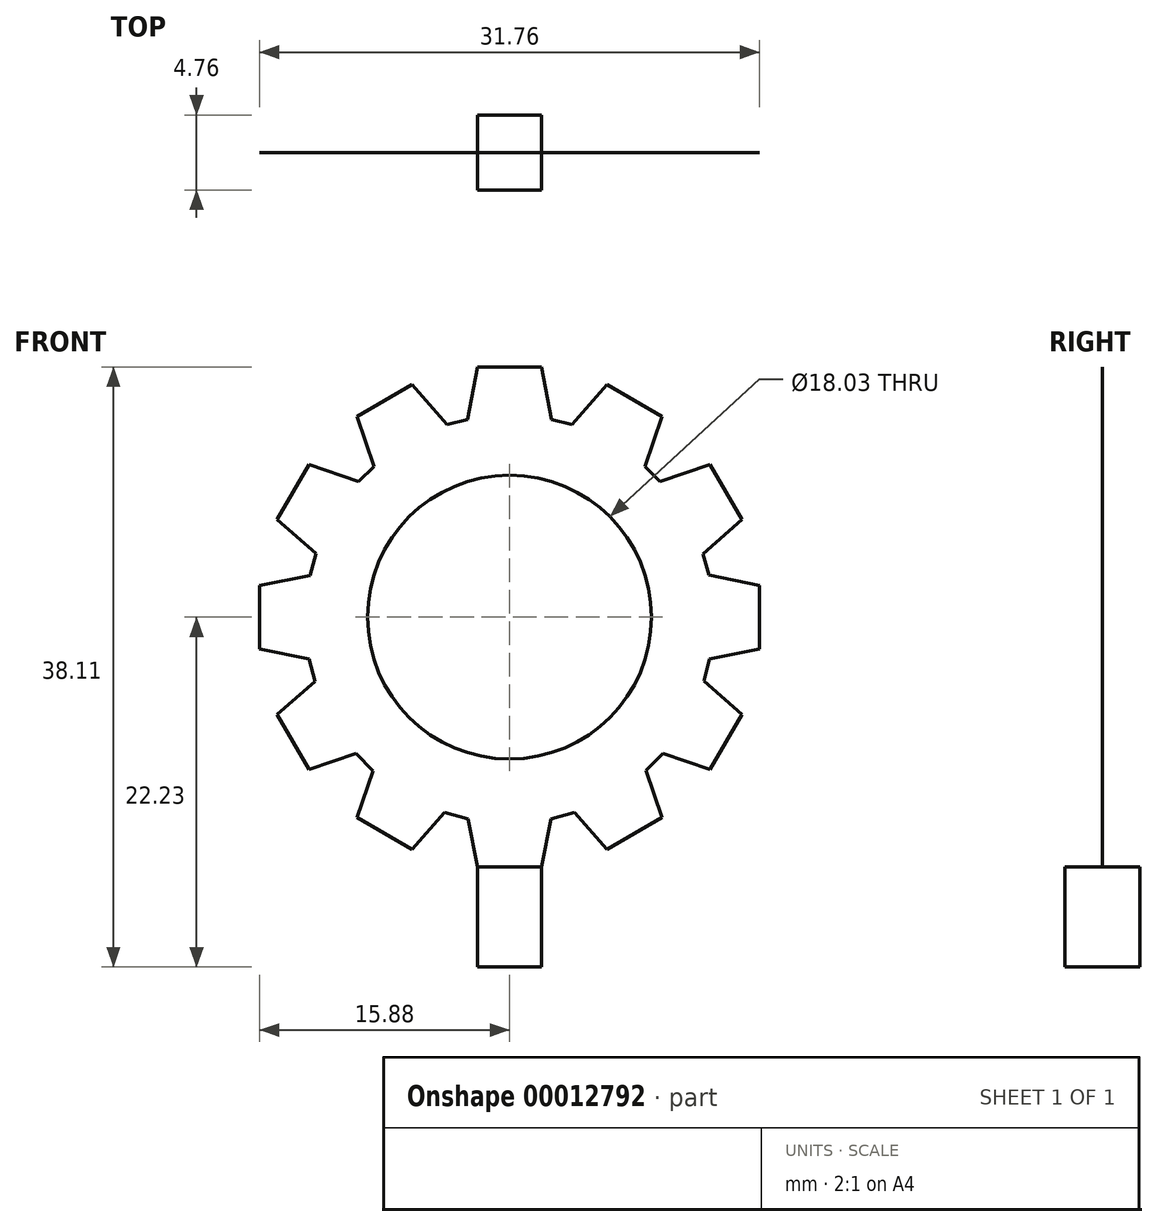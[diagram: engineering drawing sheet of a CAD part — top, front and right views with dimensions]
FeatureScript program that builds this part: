
annotation { "Feature Type Name" : "Feature", "Feature Type Description" : "" }
export const myFeature = defineFeature(function(context is Context, id is Id, definition is map)
    precondition{}
    {
        {
            var Q0;
            Q0=qCreatedBy(makeId("Front.planeOp"),FACE);
            var sketch = newSketch(context, id + "F0", { "sketchPlane" : qUnion([Q0])});
            skArc(sketch, "E0", {"start": v(0, 9.01) * mm, "mid": v(-6.37, 6.37) * mm, "end": v(-9.01, 0) * mm});
            skArc(sketch, "E1", {"start": v(-9.01, 0) * mm, "mid": v(-6.37, -6.37) * mm, "end": v(0, -9.01) * mm});
            skArc(sketch, "E2", {"start": v(0, -9.01) * mm, "mid": v(6.37, -6.37) * mm, "end": v(9.01, 0) * mm});
            skArc(sketch, "E3", {"start": v(9.01, 0) * mm, "mid": v(6.37, 6.37) * mm, "end": v(0, 9.01) * mm});
            skLineSegment(sketch, "E4", {"start": v(12.28, 4.01) * mm, "end": v(14.76, 6.19) * mm});
            skLineSegment(sketch, "E5", {"start": v(14.76, 6.19) * mm, "end": v(12.74, 9.69) * mm});
            skLineSegment(sketch, "E6", {"start": v(12.74, 9.69) * mm, "end": v(9.57, 8.6) * mm});
            skLineSegment(sketch, "E7", {"start": v(9.57, 8.6) * mm, "end": v(8.6, 9.56) * mm});
            skLineSegment(sketch, "E8", {"start": v(8.6, 9.56) * mm, "end": v(9.69, 12.74) * mm});
            skLineSegment(sketch, "E9", {"start": v(9.69, 12.74) * mm, "end": v(6.19, 14.76) * mm});
            skLineSegment(sketch, "E10", {"start": v(6.19, 14.76) * mm, "end": v(3.96, 12.22) * mm});
            skLineSegment(sketch, "E11", {"start": v(3.96, 12.22) * mm, "end": v(2.68, 12.56) * mm});
            skLineSegment(sketch, "E12", {"start": v(2.68, 12.56) * mm, "end": v(2.02, 15.88) * mm});
            skLineSegment(sketch, "E13", {"start": v(2.02, 15.88) * mm, "end": v(-2.02, 15.88) * mm});
            skLineSegment(sketch, "E14", {"start": v(-2.02, 15.88) * mm, "end": v(-2.68, 12.56) * mm});
            skLineSegment(sketch, "E15", {"start": v(-2.68, 12.56) * mm, "end": v(-3.97, 12.22) * mm});
            skLineSegment(sketch, "E16", {"start": v(-3.97, 12.22) * mm, "end": v(-6.19, 14.76) * mm});
            skLineSegment(sketch, "E17", {"start": v(-6.19, 14.76) * mm, "end": v(-9.69, 12.74) * mm});
            skLineSegment(sketch, "E18", {"start": v(-9.69, 12.74) * mm, "end": v(-8.61, 9.57) * mm});
            skLineSegment(sketch, "E19", {"start": v(-8.61, 9.57) * mm, "end": v(-9.58, 8.62) * mm});
            skLineSegment(sketch, "E20", {"start": v(-9.58, 8.62) * mm, "end": v(-12.74, 9.69) * mm});
            skLineSegment(sketch, "E21", {"start": v(-12.74, 9.69) * mm, "end": v(-14.76, 6.19) * mm});
            skLineSegment(sketch, "E22", {"start": v(-14.76, 6.19) * mm, "end": v(-12.3, 4.03) * mm});
            skLineSegment(sketch, "E23", {"start": v(-12.3, 4.03) * mm, "end": v(-12.68, 2.66) * mm});
            skLineSegment(sketch, "E24", {"start": v(-12.68, 2.66) * mm, "end": v(-15.88, 2.02) * mm});
            skLineSegment(sketch, "E25", {"start": v(-15.88, 2.02) * mm, "end": v(-15.88, -2.02) * mm});
            skLineSegment(sketch, "E26", {"start": v(-15.88, -2.02) * mm, "end": v(-12.73, -2.65) * mm});
            skLineSegment(sketch, "E27", {"start": v(-12.73, -2.65) * mm, "end": v(-12.36, -4.08) * mm});
            skLineSegment(sketch, "E28", {"start": v(-12.36, -4.08) * mm, "end": v(-14.76, -6.19) * mm});
            skLineSegment(sketch, "E29", {"start": v(-14.76, -6.19) * mm, "end": v(-12.74, -9.69) * mm});
            skLineSegment(sketch, "E30", {"start": v(-12.74, -9.69) * mm, "end": v(-9.76, -8.68) * mm});
            skLineSegment(sketch, "E31", {"start": v(-9.76, -8.68) * mm, "end": v(-8.68, -9.77) * mm});
            skLineSegment(sketch, "E32", {"start": v(-8.68, -9.77) * mm, "end": v(-9.69, -12.74) * mm});
            skLineSegment(sketch, "E33", {"start": v(-9.69, -12.74) * mm, "end": v(-6.19, -14.76) * mm});
            skLineSegment(sketch, "E34", {"start": v(-6.19, -14.76) * mm, "end": v(-4.14, -12.42) * mm});
            skLineSegment(sketch, "E35", {"start": v(-4.14, -12.42) * mm, "end": v(-2.63, -12.83) * mm});
            skLineSegment(sketch, "E36", {"start": v(-2.63, -12.83) * mm, "end": v(-2.02, -15.88) * mm});
            skLineSegment(sketch, "E37", {"start": v(-2.02, -15.88) * mm, "end": v(2.02, -15.88) * mm});
            skLineSegment(sketch, "E38", {"start": v(2.02, -15.88) * mm, "end": v(2.63, -12.82) * mm});
            skLineSegment(sketch, "E39", {"start": v(2.63, -12.82) * mm, "end": v(4.13, -12.41) * mm});
            skLineSegment(sketch, "E40", {"start": v(4.13, -12.41) * mm, "end": v(6.19, -14.76) * mm});
            skLineSegment(sketch, "E41", {"start": v(6.19, -14.76) * mm, "end": v(9.69, -12.74) * mm});
            skLineSegment(sketch, "E42", {"start": v(9.69, -12.74) * mm, "end": v(8.67, -9.75) * mm});
            skLineSegment(sketch, "E43", {"start": v(8.67, -9.75) * mm, "end": v(9.74, -8.67) * mm});
            skLineSegment(sketch, "E44", {"start": v(9.74, -8.67) * mm, "end": v(12.74, -9.69) * mm});
            skLineSegment(sketch, "E45", {"start": v(12.74, -9.69) * mm, "end": v(14.76, -6.19) * mm});
            skLineSegment(sketch, "E46", {"start": v(14.76, -6.19) * mm, "end": v(12.34, -4.07) * mm});
            skLineSegment(sketch, "E47", {"start": v(12.34, -4.07) * mm, "end": v(12.7, -2.65) * mm});
            skLineSegment(sketch, "E48", {"start": v(12.7, -2.65) * mm, "end": v(15.87, -2.02) * mm});
            skLineSegment(sketch, "E49", {"start": v(15.87, -2.02) * mm, "end": v(15.88, 2.02) * mm});
            skLineSegment(sketch, "E50", {"start": v(15.88, 2.02) * mm, "end": v(12.65, 2.66) * mm});
            skLineSegment(sketch, "E51", {"start": v(12.65, 2.66) * mm, "end": v(12.28, 4.01) * mm});
            skSolve(sketch);
        }
        {
            var Q0;
            Q0=makeQuery(id+"F0.imprint","IMPRINT",FACE,{"disambiguationData":[TD([[makeQuery(id+"F0.imprint","IMPRINT",EDGE,{"derivedFrom":sQuery(id+"F0.wireOp",EDGE,"E0")}),-1.0]])]});
            extrude(context, id + "F1", {"entities" : qUnion([Q0]), "oppositeDirection" : true, "depth" : 3 / 406.4 * mm});
        }
        {
            var Q0;
            Q0=makeQuery(id+"F1.opExtrude","SWEPT_BODY",BODY,{"disambiguationData":[OSD([sQuery(id+"F0.wireOp",EDGE,"E0"),sQuery(id+"F0.wireOp",EDGE,"E1"),sQuery(id+"F0.wireOp",EDGE,"E2"),sQuery(id+"F0.wireOp",EDGE,"E3"),sQuery(id+"F0.wireOp",EDGE,"E4"),sQuery(id+"F0.wireOp",EDGE,"E5"),sQuery(id+"F0.wireOp",EDGE,"E6"),sQuery(id+"F0.wireOp",EDGE,"E7"),sQuery(id+"F0.wireOp",EDGE,"E8"),sQuery(id+"F0.wireOp",EDGE,"E9"),sQuery(id+"F0.wireOp",EDGE,"E10"),sQuery(id+"F0.wireOp",EDGE,"E11"),sQuery(id+"F0.wireOp",EDGE,"E12"),sQuery(id+"F0.wireOp",EDGE,"E13"),sQuery(id+"F0.wireOp",EDGE,"E14"),sQuery(id+"F0.wireOp",EDGE,"E15"),sQuery(id+"F0.wireOp",EDGE,"E16"),sQuery(id+"F0.wireOp",EDGE,"E17"),sQuery(id+"F0.wireOp",EDGE,"E18"),sQuery(id+"F0.wireOp",EDGE,"E19"),sQuery(id+"F0.wireOp",EDGE,"E20"),sQuery(id+"F0.wireOp",EDGE,"E21"),sQuery(id+"F0.wireOp",EDGE,"E22"),sQuery(id+"F0.wireOp",EDGE,"E23"),sQuery(id+"F0.wireOp",EDGE,"E24"),sQuery(id+"F0.wireOp",EDGE,"E25"),sQuery(id+"F0.wireOp",EDGE,"E26"),sQuery(id+"F0.wireOp",EDGE,"E27"),sQuery(id+"F0.wireOp",EDGE,"E28"),sQuery(id+"F0.wireOp",EDGE,"E29"),sQuery(id+"F0.wireOp",EDGE,"E30"),sQuery(id+"F0.wireOp",EDGE,"E31"),sQuery(id+"F0.wireOp",EDGE,"E32"),sQuery(id+"F0.wireOp",EDGE,"E33"),sQuery(id+"F0.wireOp",EDGE,"E34"),sQuery(id+"F0.wireOp",EDGE,"E35"),sQuery(id+"F0.wireOp",EDGE,"E36"),sQuery(id+"F0.wireOp",EDGE,"E37"),sQuery(id+"F0.wireOp",EDGE,"E38"),sQuery(id+"F0.wireOp",EDGE,"E39"),sQuery(id+"F0.wireOp",EDGE,"E40"),sQuery(id+"F0.wireOp",EDGE,"E41"),sQuery(id+"F0.wireOp",EDGE,"E42"),sQuery(id+"F0.wireOp",EDGE,"E43"),sQuery(id+"F0.wireOp",EDGE,"E44"),sQuery(id+"F0.wireOp",EDGE,"E45"),sQuery(id+"F0.wireOp",EDGE,"E46"),sQuery(id+"F0.wireOp",EDGE,"E47"),sQuery(id+"F0.wireOp",EDGE,"E48"),sQuery(id+"F0.wireOp",EDGE,"E49"),sQuery(id+"F0.wireOp",EDGE,"E50"),sQuery(id+"F0.wireOp",EDGE,"E51")])]});
            transform(context, id + "F2", {"entities" : qUnion([Q0]), "transformType" : TransformType.TRANSLATION_3D, "dx" : 0 * mm, "dy" : -3 / 812.8 * mm, "dz" : 0 * mm, "makeCopy" : false});
        }
        {
            var Q0;
            Q0=makeQuery(id+"F1.opExtrude","SWEPT_FACE",FACE,{"disambiguationData":[OSD([sQuery(id+"F0.wireOp",EDGE,"E37")])]});
            var sketch = newSketch(context, id + "F3", { "sketchPlane" : qUnion([Q0])});
            skLineSegment(sketch, "E52.bottom", {"start": v(-2.02, 2.38) * mm, "end": v(2.02, 2.38) * mm});
            skLineSegment(sketch, "E52.top", {"start": v(-2.02, -2.38) * mm, "end": v(2.02, -2.38) * mm});
            skLineSegment(sketch, "E52.left", {"start": v(-2.02, 2.38) * mm, "end": v(-2.02, -2.38) * mm});
            skLineSegment(sketch, "E52.right", {"start": v(2.02, 2.38) * mm, "end": v(2.02, -2.38) * mm});
            skSolve(sketch);
        }
        {
            var Q0;
            Q0 = qSketchRegion(id + "F3", true);
            extrude(context, id + "F4", {"entities" : qUnion([Q0]), "operationType" : NewBodyOperationType.ADD, "depth" : 6.35 * mm});
        }
    });
